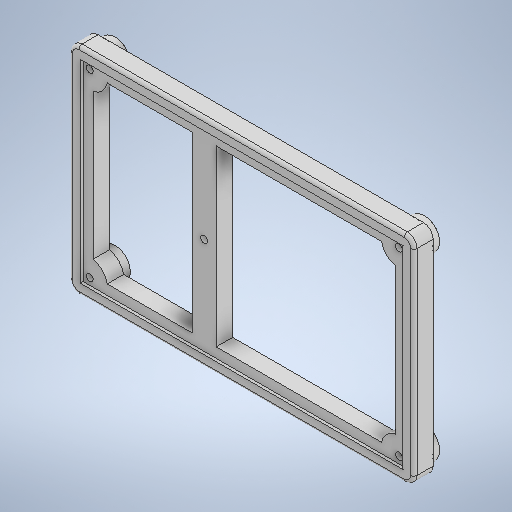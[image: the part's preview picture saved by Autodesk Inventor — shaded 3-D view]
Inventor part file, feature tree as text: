
AUTODESK INVENTOR PART (.ipt)
format: ipt  version: 2025 (Build 290162000, 162)  size: 404,480 bytes
history: native  units: in
note: dims shown in document units (in); Inventor stores cm internally (conversion verified against a paired STEP export)
features: fillet x7, sketch x7, extrude x6, hole x1
ambient origin geometry x8: Origin, YZ Plane, XZ Plane, XY Plane, X Axis, Y Axis, Z Axis, Center Point
bodies: Solid1 (feature_tree)
feature tree (21):
  extrude  "Extrusion1"  Depth=4.9606in
  extrude  "Extrusion2"  Depth=0.3543in
  hole  "Hole1"  [1 undecoded]
  extrude  "Extrusion3"  Depth=7.8898in
  extrude  "Extrusion4"  Depth=0.0709in TaperAngle=0.0deg
  fillet  "Fillet1"  Radius=3.7795in
  fillet  "Fillet2"  Radius=2.2047in
  fillet  "Fillet3"  Radius=3.7795in
  extrude  "Extrusion7"  Depth=3.7795in
  extrude  "Extrusion8"  Depth=0.0276in
  fillet  "Fillet4"  Radius=2.2047in
  fillet  "Fillet5"  Radius=0.9843in
  fillet  "Fillet6"  [1 undecoded]
  fillet  "Fillet7"  Radius=0.1575in
  sketch  "Sketch1"  dims[d0=8.1102in d1=4.9606in]
  sketch  "Sketch2"  dims[d2=0.3543in d3=0.3543in]
  sketch  "Sketch3"  dims[d4=0.5906in d5=0.689in]
  sketch  "Sketch4"  dims[d6=0.4724in d7=0.0in d8=7.8898in]
  sketch  "Sketch5"  dims[d9=4.7402in d10=0.0709in d11=0.0in d12=3.7795in d13=2.2047in d14=3.7795in]
  sketch  "Sketch9"  dims[d15=2.2047in d16=3.7795in]
  sketch  "Sketch10"  dims[d17=2.2047in d18=3.7795in d19=2.2047in d20=0.1701in d21=0.2362in d22=0.1732in d23=0.0787in d24=90.0deg d25=0.315in d26=0.8108in d27=0.9843in d28=0.0in d29=0.1575in d30=0.1575in d31=0.3937in d32=0.0in d33=0.3937in d34=0.0in d47=0.2362in d48=0.2362in d49=0.0787in d51=0.2362in d52=-0.1031in d53=0.6575in d54=0.6575in d55=0.6575in d56=0.6575in d57=0.0591in d58=0.0in d59=0.0276in d60=0.0276in d61=0.0276in d62=0.0276in]
note: 2 required parameter values undecoded (feature->parameter linkage not recoverable at this tier; creation-order binding heuristic only, values carry confidence <= 0.55)
